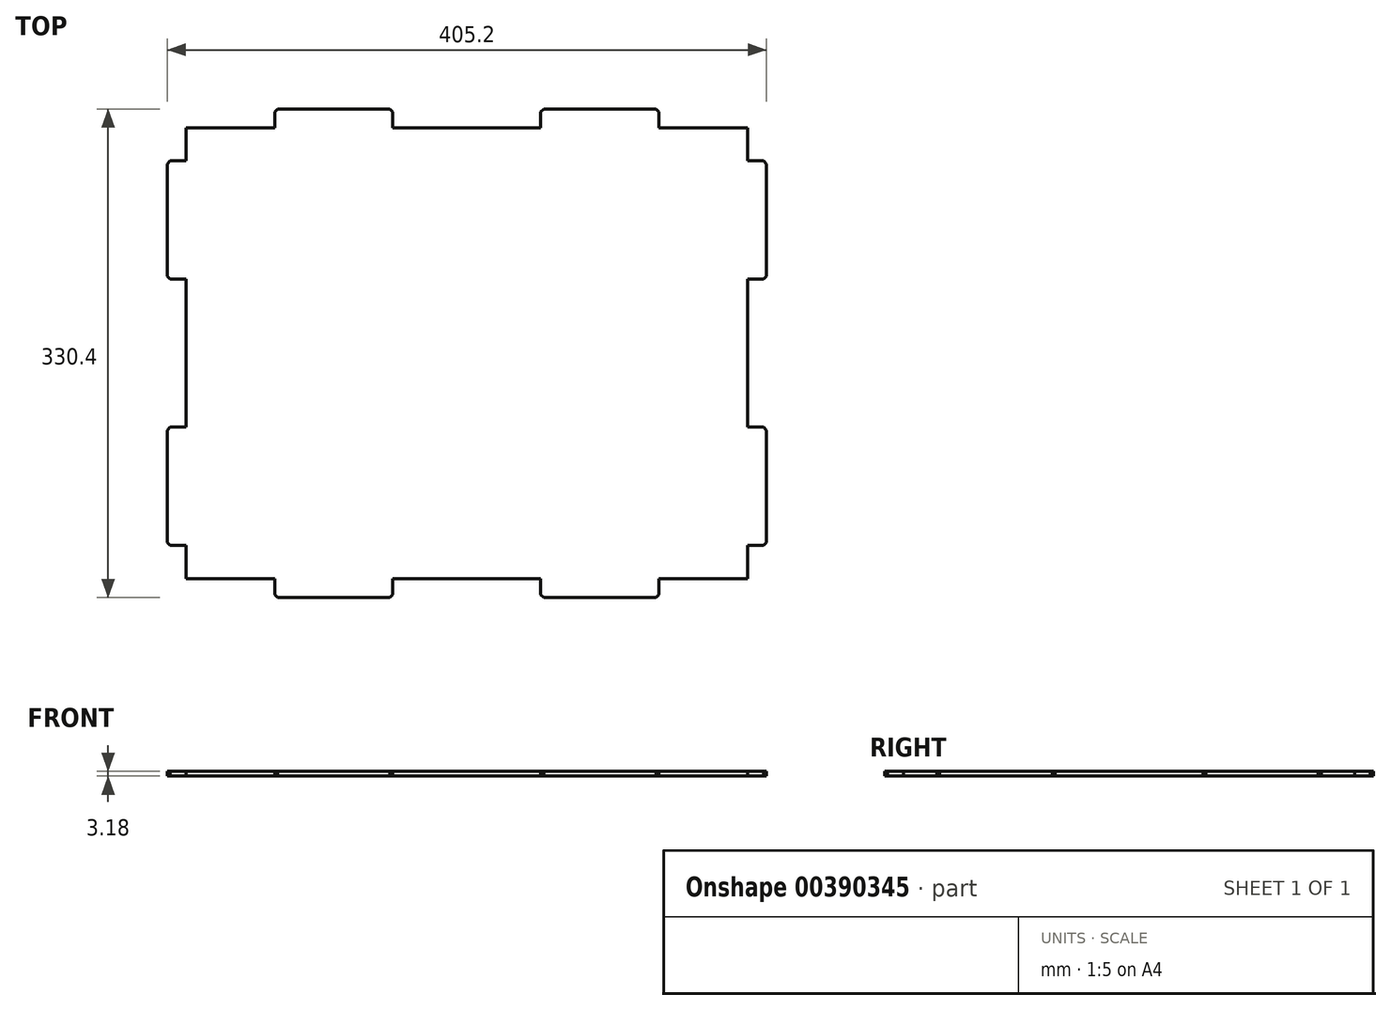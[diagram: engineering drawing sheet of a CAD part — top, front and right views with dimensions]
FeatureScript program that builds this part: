
annotation { "Feature Type Name" : "Feature", "Feature Type Description" : "" }
export const myFeature = defineFeature(function(context is Context, id is Id, definition is map)
    precondition{}
    {
        {
            assignVariable(context, id + "F0", {"name" : "MW2", "anyValue" : 3.18});
        }
        {
            var Q0;
            Q0=qCreatedBy(makeId("Top.planeOp"),FACE);
            var sketch = newSketch(context, id + "F1", { "sketchPlane" : qUnion([Q0])});
            skLineSegment(sketch, "E0.bottom", {"start": v(-189.9, -152.5) * mm, "end": v(-130, -152.5) * mm});
            skLineSegment(sketch, "E0.top", {"start": v(-189.9, 152.5) * mm, "end": v(-130, 152.5) * mm});
            skLineSegment(sketch, "E0.left", {"start": v(-189.9, -152.5) * mm, "end": v(-189.9, -130) * mm});
            skLineSegment(sketch, "E0.right", {"start": v(189.9, -152.5) * mm, "end": v(189.9, -130) * mm});
            skPoint(sketch, "E0.middle", {"position": v(0, 0) * mm});
            skLineSegment(sketch, "E1.bottom", {"start": v(-189.9, 130) * mm, "end": v(-202.6, 130) * mm});
            skLineSegment(sketch, "E1.top", {"start": v(-189.9, 50) * mm, "end": v(-202.6, 50) * mm});
            skLineSegment(sketch, "E1.right", {"start": v(-202.6, 130) * mm, "end": v(-202.6, 50) * mm});
            skLineSegment(sketch, "E2.top", {"start": v(-130, 165.2) * mm, "end": v(-50, 165.2) * mm});
            skLineSegment(sketch, "E2.left", {"start": v(-130, 152.5) * mm, "end": v(-130, 165.2) * mm});
            skLineSegment(sketch, "E2.right", {"start": v(-50, 152.5) * mm, "end": v(-50, 165.2) * mm});
            skLineSegment(sketch, "E3.trimOffspring", {"start": v(-189.9, 130) * mm, "end": v(-189.9, 152.5) * mm});
            skLineSegment(sketch, "E4.trimOffspring", {"start": v(-50, 152.5) * mm, "end": v(50, 152.5) * mm});
            skLineSegment(sketch, "E5.MirrorCS", {"start": v(-189.9, -130) * mm, "end": v(-202.6, -130) * mm});
            skLineSegment(sketch, "E6.MirrorCS", {"start": v(-202.6, -130) * mm, "end": v(-202.6, -50) * mm});
            skLineSegment(sketch, "E7.MirrorCS", {"start": v(-189.9, -50) * mm, "end": v(-202.6, -50) * mm});
            skLineSegment(sketch, "E8.MirrorCS", {"start": v(130, 152.5) * mm, "end": v(130, 165.2) * mm});
            skLineSegment(sketch, "E9.MirrorCS", {"start": v(130, 165.2) * mm, "end": v(50, 165.2) * mm});
            skLineSegment(sketch, "E10.MirrorCS", {"start": v(50, 152.5) * mm, "end": v(50, 165.2) * mm});
            skLineSegment(sketch, "E11.MirrorCS", {"start": v(-50, -152.5) * mm, "end": v(-50, -165.2) * mm});
            skLineSegment(sketch, "E12.MirrorCS", {"start": v(-130, -165.2) * mm, "end": v(-50, -165.2) * mm});
            skLineSegment(sketch, "E13.MirrorCS", {"start": v(-130, -152.5) * mm, "end": v(-130, -165.2) * mm});
            skLineSegment(sketch, "E14.MirrorCS", {"start": v(130, -165.2) * mm, "end": v(50, -165.2) * mm});
            skLineSegment(sketch, "E15.MirrorCS", {"start": v(130, -152.5) * mm, "end": v(130, -165.2) * mm});
            skLineSegment(sketch, "E16.MirrorCS", {"start": v(50, -152.5) * mm, "end": v(50, -165.2) * mm});
            skLineSegment(sketch, "E17.MirrorCS", {"start": v(189.9, -130) * mm, "end": v(202.6, -130) * mm});
            skLineSegment(sketch, "E18.MirrorCS", {"start": v(189.9, -50) * mm, "end": v(202.6, -50) * mm});
            skLineSegment(sketch, "E19.MirrorCS", {"start": v(202.6, -130) * mm, "end": v(202.6, -50) * mm});
            skLineSegment(sketch, "E20.MirrorCS", {"start": v(189.9, 50) * mm, "end": v(202.6, 50) * mm});
            skLineSegment(sketch, "E21.MirrorCS", {"start": v(202.6, 130) * mm, "end": v(202.6, 50) * mm});
            skLineSegment(sketch, "E22.MirrorCS", {"start": v(189.9, 130) * mm, "end": v(202.6, 130) * mm});
            skLineSegment(sketch, "E23.trimOffspring", {"start": v(189.9, 130) * mm, "end": v(189.9, 152.5) * mm});
            skLineSegment(sketch, "E24.trimOffspring", {"start": v(130, 152.5) * mm, "end": v(189.9, 152.5) * mm});
            skLineSegment(sketch, "E25.trimOffspring", {"start": v(130, -152.5) * mm, "end": v(189.9, -152.5) * mm});
            skLineSegment(sketch, "E26.trimOffspring", {"start": v(189.9, -50) * mm, "end": v(189.9, 50) * mm});
            skLineSegment(sketch, "E27.trimOffspring", {"start": v(-50, -152.5) * mm, "end": v(50, -152.5) * mm});
            skLineSegment(sketch, "E28.trimOffspring", {"start": v(-189.9, -50) * mm, "end": v(-189.9, 50) * mm});
            skSolve(sketch);
        }
        {
            var Q0;
            Q0 = qSketchRegion(id + "F1", true);
            extrude(context, id + "F2", {"entities" : qUnion([Q0]), "depth" : (getVariable(context, 'MW2')) * mm});
        }
        {
            var Q0;
            Q0=makeQuery(id+"F2.opExtrude","SWEPT_EDGE",EDGE,{"disambiguationData":[OSD([sQuery(id+"F1.wireOp",EDGE,"E1.top"),sQuery(id+"F1.wireOp",EDGE,"E1.right")])]});
            var Q1;
            Q1=makeQuery(id+"F2.opExtrude","SWEPT_EDGE",EDGE,{"disambiguationData":[OSD([sQuery(id+"F1.wireOp",EDGE,"E6.MirrorCS"),sQuery(id+"F1.wireOp",EDGE,"E7.MirrorCS")])]});
            var Q2;
            Q2=makeQuery(id+"F2.opExtrude","SWEPT_EDGE",EDGE,{"disambiguationData":[OSD([sQuery(id+"F1.wireOp",EDGE,"E5.MirrorCS"),sQuery(id+"F1.wireOp",EDGE,"E6.MirrorCS")])]});
            var Q3;
            Q3=makeQuery(id+"F2.opExtrude","SWEPT_EDGE",EDGE,{"disambiguationData":[OSD([sQuery(id+"F1.wireOp",EDGE,"E12.MirrorCS"),sQuery(id+"F1.wireOp",EDGE,"E13.MirrorCS")])]});
            var Q4;
            Q4=makeQuery(id+"F2.opExtrude","SWEPT_EDGE",EDGE,{"disambiguationData":[OSD([sQuery(id+"F1.wireOp",EDGE,"E11.MirrorCS"),sQuery(id+"F1.wireOp",EDGE,"E12.MirrorCS")])]});
            var Q5;
            Q5=makeQuery(id+"F2.opExtrude","SWEPT_EDGE",EDGE,{"disambiguationData":[OSD([sQuery(id+"F1.wireOp",EDGE,"E14.MirrorCS"),sQuery(id+"F1.wireOp",EDGE,"E16.MirrorCS")])]});
            var Q6;
            Q6=makeQuery(id+"F2.opExtrude","SWEPT_EDGE",EDGE,{"disambiguationData":[OSD([sQuery(id+"F1.wireOp",EDGE,"E14.MirrorCS"),sQuery(id+"F1.wireOp",EDGE,"E15.MirrorCS")])]});
            var Q7;
            Q7=makeQuery(id+"F2.opExtrude","SWEPT_EDGE",EDGE,{"disambiguationData":[OSD([sQuery(id+"F1.wireOp",EDGE,"E17.MirrorCS"),sQuery(id+"F1.wireOp",EDGE,"E19.MirrorCS")])]});
            var Q8;
            Q8=makeQuery(id+"F2.opExtrude","SWEPT_EDGE",EDGE,{"disambiguationData":[OSD([sQuery(id+"F1.wireOp",EDGE,"E18.MirrorCS"),sQuery(id+"F1.wireOp",EDGE,"E19.MirrorCS")])]});
            var Q9;
            Q9=makeQuery(id+"F2.opExtrude","SWEPT_EDGE",EDGE,{"disambiguationData":[OSD([sQuery(id+"F1.wireOp",EDGE,"E20.MirrorCS"),sQuery(id+"F1.wireOp",EDGE,"E21.MirrorCS")])]});
            var Q10;
            Q10=makeQuery(id+"F2.opExtrude","SWEPT_EDGE",EDGE,{"disambiguationData":[OSD([sQuery(id+"F1.wireOp",EDGE,"E21.MirrorCS"),sQuery(id+"F1.wireOp",EDGE,"E22.MirrorCS")])]});
            var Q11;
            Q11=makeQuery(id+"F2.opExtrude","SWEPT_EDGE",EDGE,{"disambiguationData":[OSD([sQuery(id+"F1.wireOp",EDGE,"E8.MirrorCS"),sQuery(id+"F1.wireOp",EDGE,"E9.MirrorCS")])]});
            var Q12;
            Q12=makeQuery(id+"F2.opExtrude","SWEPT_EDGE",EDGE,{"disambiguationData":[OSD([sQuery(id+"F1.wireOp",EDGE,"E9.MirrorCS"),sQuery(id+"F1.wireOp",EDGE,"E10.MirrorCS")])]});
            var Q13;
            Q13=makeQuery(id+"F2.opExtrude","SWEPT_EDGE",EDGE,{"disambiguationData":[OSD([sQuery(id+"F1.wireOp",EDGE,"E2.top"),sQuery(id+"F1.wireOp",EDGE,"E2.right")])]});
            var Q14;
            Q14=makeQuery(id+"F2.opExtrude","SWEPT_EDGE",EDGE,{"disambiguationData":[OSD([sQuery(id+"F1.wireOp",EDGE,"E2.top"),sQuery(id+"F1.wireOp",EDGE,"E2.left")])]});
            var Q15;
            Q15=makeQuery(id+"F2.opExtrude","SWEPT_EDGE",EDGE,{"disambiguationData":[OSD([sQuery(id+"F1.wireOp",EDGE,"E1.bottom"),sQuery(id+"F1.wireOp",EDGE,"E1.right")])]});
            chamfer(context, id + "F3", {"entities" : qUnion([Q0, Q1, Q2, Q3, Q4, Q5, Q6, Q7, Q8, Q9, Q10, Q11, Q12, Q13, Q14, Q15]), "width" : 2 * mm, "tangentPropagation" : true});
        }
    });
